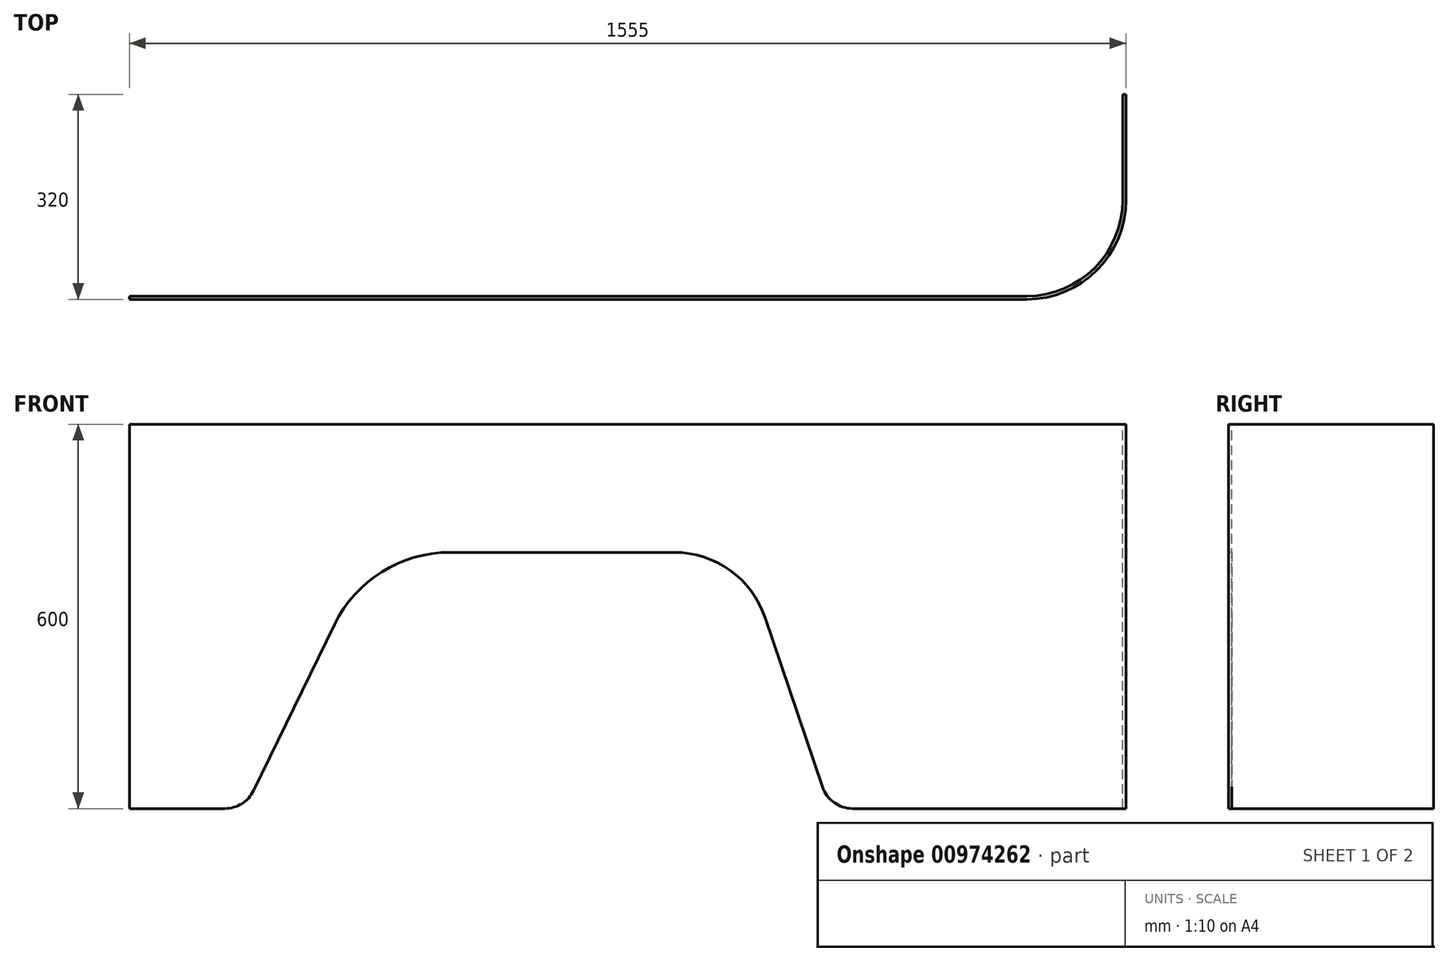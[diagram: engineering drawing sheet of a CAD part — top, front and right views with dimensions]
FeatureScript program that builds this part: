
annotation { "Feature Type Name" : "Feature", "Feature Type Description" : "" }
export const myFeature = defineFeature(function(context is Context, id is Id, definition is map)
    precondition{}
    {
        {
            var Q0;
            Q0=qCreatedBy(makeId("Top.planeOp"),FACE);
            var sketch = newSketch(context, id + "F0", { "sketchPlane" : qUnion([Q0])});
            skLineSegment(sketch, "E0", {"start": v(0, 0) * mm, "end": v(1400, 0) * mm});
            skArc(sketch, "E1", {"start": v(1400, 0) * mm, "mid": v(1509.6, 45.4) * mm, "end": v(1555, 155) * mm});
            skLineSegment(sketch, "E2", {"start": v(1555, 155) * mm, "end": v(1555, 320) * mm});
            skLineSegment(sketch, "E3.0", {"start": v(0, 5) * mm, "end": v(1400, 5) * mm});
            skArc(sketch, "E4.0", {"start": v(1400, 5) * mm, "mid": v(1506.07, 48.93) * mm, "end": v(1550, 155) * mm});
            skLineSegment(sketch, "E5.0", {"start": v(1550, 155) * mm, "end": v(1550, 320) * mm});
            skLineSegment(sketch, "E6", {"start": v(0, 0) * mm, "end": v(0, 5) * mm});
            skLineSegment(sketch, "E7", {"start": v(1555, 320) * mm, "end": v(1550, 320) * mm});
            skSolve(sketch);
        }
        {
            var Q0;
            Q0=makeQuery(id+"F0.imprint","IMPRINT",FACE,{"disambiguationData":[TD([[makeQuery(id+"F0.imprint","IMPRINT",EDGE,{"derivedFrom":sQuery(id+"F0.wireOp",EDGE,"E0")}),1.0]])]});
            extrude(context, id + "F1", {"entities" : qUnion([Q0]), "oppositeDirection" : true, "depth" : 600 * mm, "offsetDistance" : 25 * mm});
        }
        {
            var Q0;
            Q0=makeQuery(id+"F1.opExtrude","SWEPT_FACE",FACE,{"disambiguationData":[OSD([sQuery(id+"F0.wireOp",EDGE,"E0")])]});
            var sketch = newSketch(context, id + "F2", { "sketchPlane" : qUnion([Q0])});
            skLineSegment(sketch, "E8", {"start": v(193.69, -571.89) * mm, "end": v(320, -312.45) * mm});
            skLineSegment(sketch, "E9", {"start": v(499.82, -200) * mm, "end": v(849.82, -200) * mm});
            skLineSegment(sketch, "E10", {"start": v(991.9, -301.9) * mm, "end": v(1081.3, -566.03) * mm});
            skArc(sketch, "E11", {"start": v(499.82, -200) * mm, "mid": v(393.78, -230.43) * mm, "end": v(320, -312.45) * mm});
            skArc(sketch, "E12", {"start": v(991.9, -301.9) * mm, "mid": v(937.24, -228.11) * mm, "end": v(849.82, -200) * mm});
            skArc(sketch, "E13", {"start": v(148.73, -600) * mm, "mid": v(175.24, -592.4) * mm, "end": v(193.69, -571.89) * mm});
            skPoint(sketch, "E13.first.point", {"position": v(193.69, -571.89) * mm});
            skPoint(sketch, "E13.second.point", {"position": v(148.73, -600) * mm});
            skPoint(sketch, "E13.third.point", {"position": v(144.03, -500.22) * mm});
            skArc(sketch, "E14", {"start": v(1081.3, -566.03) * mm, "mid": v(1099.52, -590.63) * mm, "end": v(1128.67, -600) * mm});
            skPoint(sketch, "E14.first.point", {"position": v(1081.3, -566.03) * mm});
            skPoint(sketch, "E14.second.point", {"position": v(1128.67, -600) * mm});
            skPoint(sketch, "E14.third.point", {"position": v(1153.26, -506.47) * mm});
            skPoint(sketch, "E15.orphan", {"position": v(180, -600) * mm});
            skLineSegment(sketch, "E16", {"start": v(148.73, -600) * mm, "end": v(1128.67, -600) * mm});
            skSolve(sketch);
        }
        {
            var Q0;
            Q0=makeQuery(id+"F2.imprint","IMPRINT",FACE,{"disambiguationData":[TD([[makeQuery(id+"F2.imprint","IMPRINT",EDGE,{"derivedFrom":sQuery(id+"F2.wireOp",EDGE,"E8")}),-1.0]])]});
            extrude(context, id + "F3", {"entities" : qUnion([Q0]), "operationType" : NewBodyOperationType.REMOVE, "oppositeDirection" : true, "depth" : 5 * mm, "offsetDistance" : 25 * mm});
        }
    });
